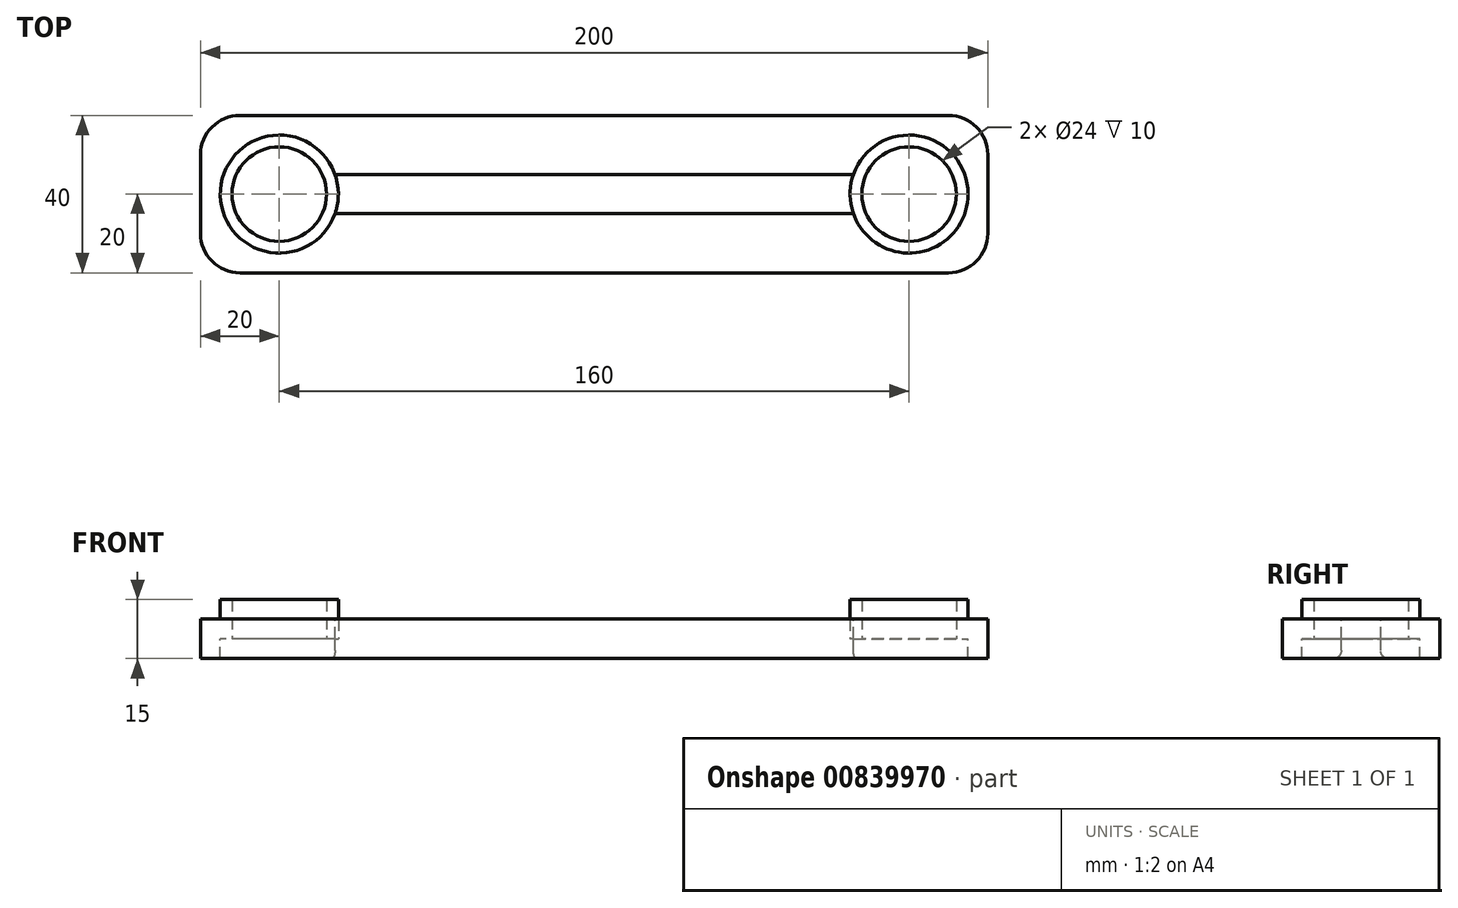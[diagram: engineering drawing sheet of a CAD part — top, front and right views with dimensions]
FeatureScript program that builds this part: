
annotation { "Feature Type Name" : "Feature", "Feature Type Description" : "" }
export const myFeature = defineFeature(function(context is Context, id is Id, definition is map)
    precondition{}
    {
        {
            var Q0;
            Q0=qCreatedBy(makeId("Top.planeOp"),FACE);
            var sketch = newSketch(context, id + "F0", { "sketchPlane" : qUnion([Q0])});
            skLineSegment(sketch, "E0.bottom", {"start": v(-100, 20) * mm, "end": v(100, 20) * mm});
            skLineSegment(sketch, "E0.top", {"start": v(-100, -20) * mm, "end": v(100, -20) * mm});
            skLineSegment(sketch, "E0.left", {"start": v(-100, 20) * mm, "end": v(-100, -20) * mm});
            skLineSegment(sketch, "E0.right", {"start": v(100, 20) * mm, "end": v(100, -20) * mm});
            skSolve(sketch);
        }
        {
            var Q0;
            Q0 = qSketchRegion(id + "F0", true);
            extrude(context, id + "F1", {"entities" : qUnion([Q0]), "depth" : 10 * mm, "offsetDistance" : 25 * mm});
        }
        {
            var Q0;
            Q0=makeQuery(id+"F1.opExtrude","CAP_FACE",FACE,{"disambiguationData":[OSD([sQuery(id+"F0.wireOp",EDGE,"E0.bottom"),sQuery(id+"F0.wireOp",EDGE,"E0.top"),sQuery(id+"F0.wireOp",EDGE,"E0.left"),sQuery(id+"F0.wireOp",EDGE,"E0.right")])],"isStart":false});
            var sketch = newSketch(context, id + "F2", { "sketchPlane" : qUnion([Q0])});
            skCircle(sketch, "E1", {"center": v(80, 0) * mm, "radius": 15 * mm});
            skCircle(sketch, "E2", {"center": v(-80, 0) * mm, "radius": 15 * mm});
            skSolve(sketch);
        }
        {
            var Q0;
            Q0 = qSketchRegion(id + "F2", true);
            extrude(context, id + "F3", {"entities" : qUnion([Q0]), "operationType" : NewBodyOperationType.REMOVE, "oppositeDirection" : true, "depth" : 10 * mm, "offsetDistance" : 25 * mm});
        }
        {
            var Q0;
            Q0=makeQuery(id+"F1.opExtrude","CAP_FACE",FACE,{"disambiguationData":[OSD([sQuery(id+"F0.wireOp",EDGE,"E0.bottom"),sQuery(id+"F0.wireOp",EDGE,"E0.top"),sQuery(id+"F0.wireOp",EDGE,"E0.left"),sQuery(id+"F0.wireOp",EDGE,"E0.right")])],"isStart":false});
            var sketch = newSketch(context, id + "F4", { "sketchPlane" : qUnion([Q0])});
            skLineSegment(sketch, "E3.bottom", {"start": v(90, -5) * mm, "end": v(-90, -5) * mm});
            skLineSegment(sketch, "E3.top", {"start": v(90, 5) * mm, "end": v(-90, 5) * mm});
            skLineSegment(sketch, "E3.left", {"start": v(90, -5) * mm, "end": v(90, 5) * mm});
            skLineSegment(sketch, "E3.right", {"start": v(-90, -5) * mm, "end": v(-90, 5) * mm});
            skSolve(sketch);
        }
        {
            var Q0;
            {var subQ0=sQuery(id+"F4.wireOp",EDGE,"E3.bottom");var subQ1=makeQuery(id+"F3.boolean.opBoolean","COPY",EDGE,{"derivedFrom":makeQuery(id+"F3.opExtrude","CAP_EDGE",EDGE,{"disambiguationData":[OSD([sQuery(id+"F2.wireOp",EDGE,"E1")])],"isStart":true})});var subQ2=makeQuery(id+"F4.imprint","INTERSECT",VERTEX,{"derivedFrom":[subQ1,subQ0]});Q0=makeQuery(id+"F4.imprint","IMPRINT",FACE,{"disambiguationData":[TD([[makeQuery(id+"F4.imprint","IMPRINT",EDGE,{"disambiguationData":[TD([[subQ2,-1.0]])],"derivedFrom":subQ0}),-1.0]])]});}
            extrude(context, id + "F5", {"entities" : qUnion([Q0]), "operationType" : NewBodyOperationType.REMOVE, "oppositeDirection" : true, "depth" : 25 * mm, "offsetDistance" : 25 * mm});
        }
        {
            var Q0;
            Q0=makeQuery(id+"F1.opExtrude","CAP_FACE",FACE,{"disambiguationData":[OSD([sQuery(id+"F0.wireOp",EDGE,"E0.bottom"),sQuery(id+"F0.wireOp",EDGE,"E0.top"),sQuery(id+"F0.wireOp",EDGE,"E0.left"),sQuery(id+"F0.wireOp",EDGE,"E0.right")])],"isStart":false});
            var sketch = newSketch(context, id + "F6", { "sketchPlane" : qUnion([Q0])});
            skCircle(sketch, "E4", {"center": v(-80, 0) * mm, "radius": 15 * mm});
            skCircle(sketch, "E5", {"center": v(-80, 0) * mm, "radius": 12 * mm});
            skCircle(sketch, "E6", {"center": v(80, 0) * mm, "radius": 12 * mm});
            skCircle(sketch, "E7", {"center": v(80, 0) * mm, "radius": 15 * mm});
            skSolve(sketch);
        }
        {
            var Q0;
            Q0 = qSketchRegion(id + "F6", true);
            extrude(context, id + "F7", {"entities" : qUnion([Q0]), "operationType" : NewBodyOperationType.ADD, "depth" : 5 * mm, "offsetDistance" : 25 * mm, "hasSecondDirection" : true, "secondDirectionOppositeDirection" : true, "secondDirectionDepth" : 5 * mm});
        }
        {
            var Q0;
            Q0=makeQuery(id+"F1.opExtrude","SWEPT_EDGE",EDGE,{"disambiguationData":[OSD([sQuery(id+"F0.wireOp",EDGE,"E0.top"),sQuery(id+"F0.wireOp",EDGE,"E0.left")])]});
            var Q1;
            Q1=makeQuery(id+"F1.opExtrude","SWEPT_EDGE",EDGE,{"disambiguationData":[OSD([sQuery(id+"F0.wireOp",EDGE,"E0.top"),sQuery(id+"F0.wireOp",EDGE,"E0.right")])]});
            var Q2;
            Q2=makeQuery(id+"F1.opExtrude","SWEPT_EDGE",EDGE,{"disambiguationData":[OSD([sQuery(id+"F0.wireOp",EDGE,"E0.bottom"),sQuery(id+"F0.wireOp",EDGE,"E0.right")])]});
            var Q3;
            Q3=makeQuery(id+"F1.opExtrude","SWEPT_EDGE",EDGE,{"disambiguationData":[OSD([sQuery(id+"F0.wireOp",EDGE,"E0.bottom"),sQuery(id+"F0.wireOp",EDGE,"E0.left")])]});
            fillet(context, id + "F8", {"entities" : qUnion([Q0, Q1, Q2, Q3]), "radius" : 10 * mm, "tangentPropagation" : true, "allowEdgeOverflow" : false});
        }
        {
            var Q0;
            Q0=makeQuery(id+"F5.boolean.opBoolean","INTERSECT",EDGE,{"derivedFrom":[makeQuery(id+"F1.opExtrude","CAP_FACE",FACE,{"disambiguationData":[OSD([sQuery(id+"F0.wireOp",EDGE,"E0.bottom"),sQuery(id+"F0.wireOp",EDGE,"E0.top"),sQuery(id+"F0.wireOp",EDGE,"E0.left"),sQuery(id+"F0.wireOp",EDGE,"E0.right")])],"isStart":true}),makeQuery(id+"F5.opExtrude","SWEPT_FACE",FACE,{"disambiguationData":[OSD([sQuery(id+"F4.wireOp",EDGE,"E3.bottom")])]})]});
            var Q1;
            Q1=makeQuery(id+"F5.boolean.opBoolean","INTERSECT",EDGE,{"derivedFrom":[makeQuery(id+"F1.opExtrude","CAP_FACE",FACE,{"disambiguationData":[OSD([sQuery(id+"F0.wireOp",EDGE,"E0.bottom"),sQuery(id+"F0.wireOp",EDGE,"E0.top"),sQuery(id+"F0.wireOp",EDGE,"E0.left"),sQuery(id+"F0.wireOp",EDGE,"E0.right")])],"isStart":true}),makeQuery(id+"F5.opExtrude","SWEPT_FACE",FACE,{"disambiguationData":[OSD([sQuery(id+"F4.wireOp",EDGE,"E3.top")])]})]});
            fillet(context, id + "F9", {"entities" : qUnion([Q0, Q1]), "radius" : 2 * mm, "tangentPropagation" : true, "allowEdgeOverflow" : false});
        }
    });
